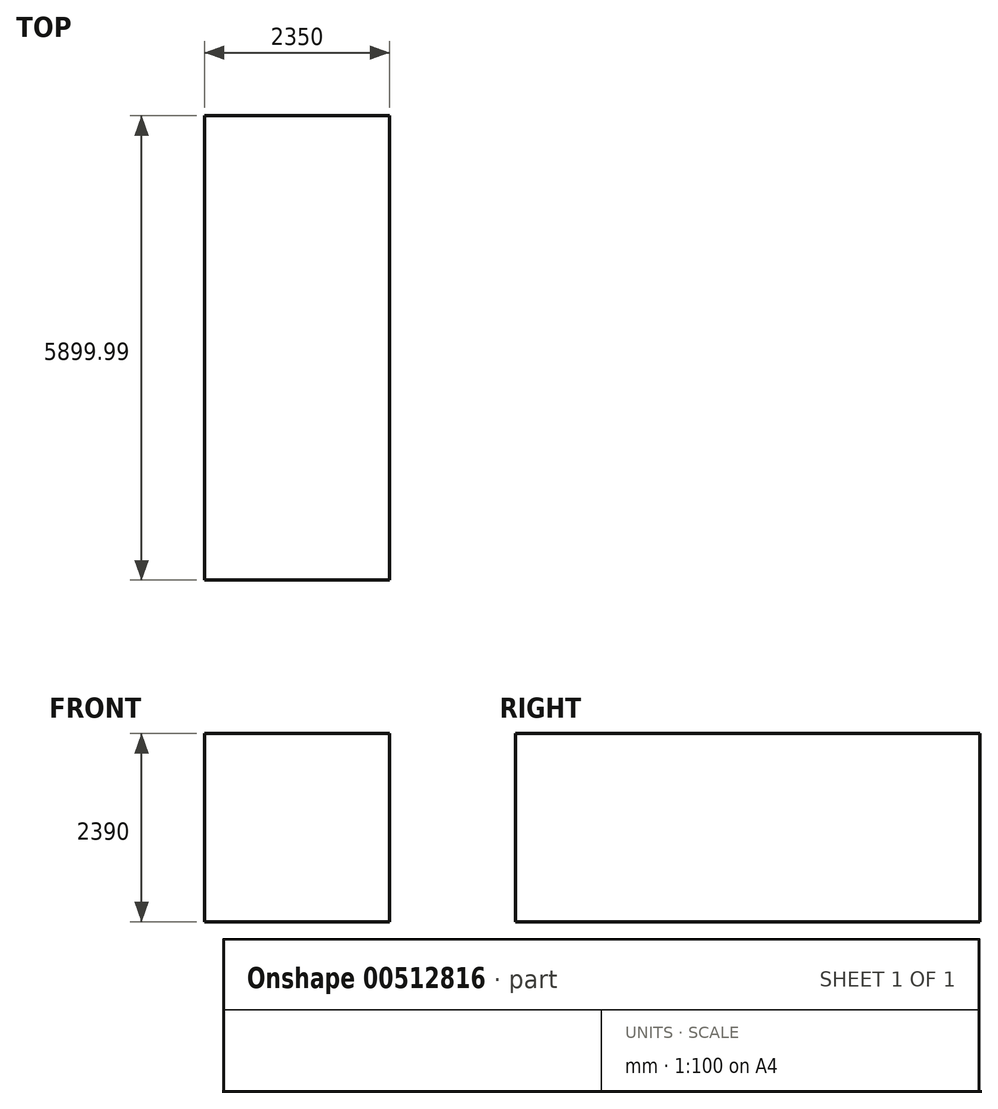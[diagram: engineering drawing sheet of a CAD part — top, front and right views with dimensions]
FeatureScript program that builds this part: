
annotation { "Feature Type Name" : "Feature", "Feature Type Description" : "" }
export const myFeature = defineFeature(function(context is Context, id is Id, definition is map)
    precondition{}
    {
        {
            var Q0;
            Q0=qCreatedBy(makeId("Front.planeOp"),FACE);
            var sketch = newSketch(context, id + "F0", { "sketchPlane" : qUnion([Q0])});
            skLineSegment(sketch, "E0.bottom", {"start": v(-1181.53, 1545.04) * mm, "end": v(1168.47, 1545.04) * mm});
            skLineSegment(sketch, "E0.top", {"start": v(-1181.53, -844.96) * mm, "end": v(1168.47, -844.96) * mm});
            skLineSegment(sketch, "E0.left", {"start": v(-1181.53, 1545.04) * mm, "end": v(-1181.53, -844.96) * mm});
            skLineSegment(sketch, "E0.right", {"start": v(1168.47, 1545.04) * mm, "end": v(1168.47, -844.96) * mm});
            skSolve(sketch);
        }
        {
            var Q0;
            Q0=makeQuery(id+"F0.imprint","IMPRINT",FACE,{"disambiguationData":[TD([[makeQuery(id+"F0.imprint","IMPRINT",EDGE,{"derivedFrom":sQuery(id+"F0.wireOp",EDGE,"E0.bottom")}),-1.0]])]});
            var Q1;
            Q1=sQuery(id+"F0.wireOp",EDGE,"E0.bottom");
            var Q2;
            Q2=sQuery(id+"F0.wireOp",EDGE,"E0.right");
            var Q3;
            Q3=sQuery(id+"F0.wireOp",EDGE,"E0.top");
            var Q4;
            Q4=sQuery(id+"F0.wireOp",EDGE,"E0.left");
            extrude(context, id + "F1", {"entities" : qUnion([Q0]), "bodyType" : ToolBodyType.SURFACE, "operationType" : NewBodyOperationType.ADD, "surfaceEntities" : qUnion([Q1, Q2, Q3, Q4]), "depth" : 5899.99 * mm});
        }
    });
